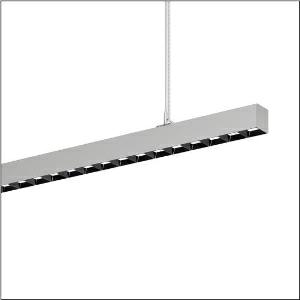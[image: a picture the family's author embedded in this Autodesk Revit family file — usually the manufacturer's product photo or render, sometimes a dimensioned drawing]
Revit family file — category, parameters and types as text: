
# Revit family: silica_r__21_51mx32dc3dsb_c9e6
name_source: partatom
category: Lighting Fixtures
units: mm (PartAtom-declared; Revit-internal decimal feet)

## family parameters
Cut with Voids When Loaded = No
Host = Face
Light Source = No
Part Type = Normal
Room Calculation Point = No
Round Connector Dimension = Use Diameter
Shared = No

## types (1)
- --- (1 x LED, 18220 lm, 113 W, 3000K)
    Apparent Load = 113 VA
    CIE Flux Codes = 86 99 100 59 100
    Color Rendering = 80
    Color Temperature = 3000K
    Default Elevation = 1800 mm
    Description = Silica® 21, office luminaire, primary light control with darklight reflector, of PMMA, black, CAT 2 (L<= 3000cd/m²), light emission: direct/indirect distribution, primary light characteristic: symmetric, installation type: suspended mounting, LED, rated luminous flux: 18.220lm, luminous efficacy: 161lm/W, light colour: 830, colour temperature: 3000K, with terminal, 3+2-pole, max. 2.5mm², mains connection: 220..240V, AC, 50/60Hz, rated input power: 113W, luminaire housing, of aluminium, metallic grey (RAL 9006), length: 3.004mm, width: 53mm, height: 53mm, protection rating (complete): IP20, insulation class (complete): insulation class I (protective earthing), certification: CE, permissible operating ambient temperature: 0..+35°C, standard: EN 50419, packaging unit: 1 piece
    Height = 53 mm
    Lamp = 1 x LED
    Lamp Light Flux = 18220 lm
    Lamp Power = 113 W
    Lamp count = 1
    Length = 3004 mm
    Luminous efficacy = 161 lm/W
    Manufacturer = Siteco
    ModVariant = No
    Model = 51MX32DC3DSB
    Mounting Place = Ceiling
    Mounting Type = Pendant
    Number of Poles = 1
    OnlyDefault = Yes
    Power Factor = 1
    Product Name = Silica® 21
    Product group = office luminaire | ceiling pendant
    ProductGroupID = 902
    Protection Class = Protection class I
    Protection Degree = IP 20
    RLX_Detail_Level = 1
    RLX_Emergency_Light_Flux = 0 lm
    RLX_Emergency_Type = 0
    RLX_Emergency_Type_DB = No
    RlxData = <blob elided: 65449 chars, md5=2f984a0c>
    Socket = socket
    Standby Power = 0 W
    System Light Flux = 18220 lm
    System Power = 113 W
    Type Comments = factory setting: luminous flux: 100 % | dim-lin: 254 | 391 mA
    Type Image = l_1335859.jpg
    URL = http://relux.com
    VarID = @adj_091445
    Voltage = 0 V
    Weight = 0.00 kg
    Width = 53 mm

## geometry (parser evidence)
native form markers: Blend x4, Sweep x12
no freeform markers — native parametric forms only
